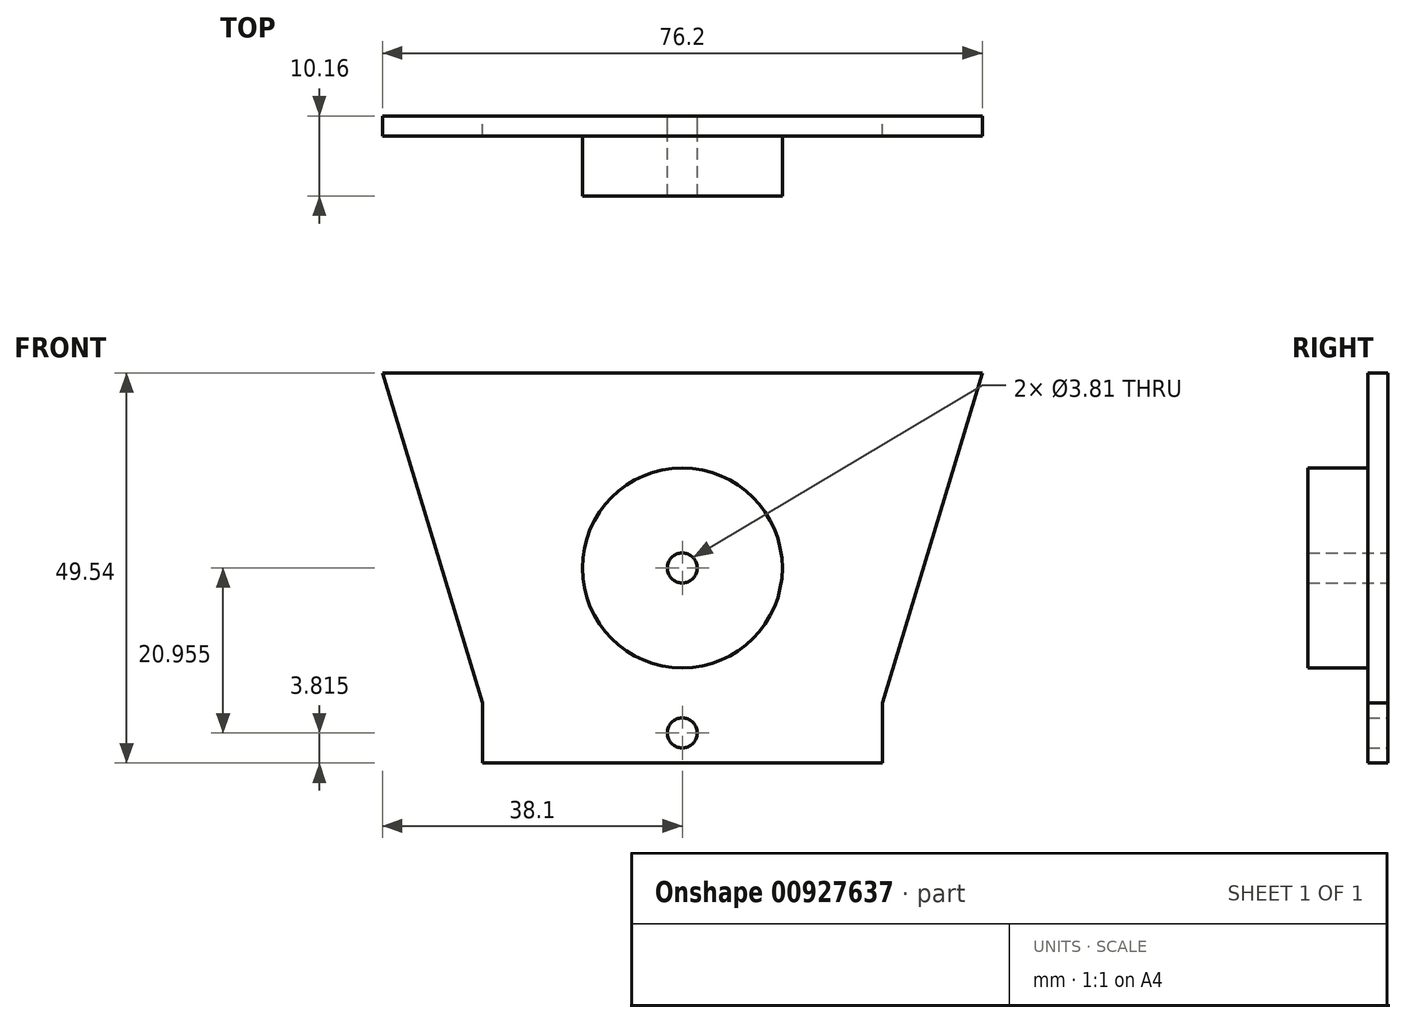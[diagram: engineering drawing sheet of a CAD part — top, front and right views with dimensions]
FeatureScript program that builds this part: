
annotation { "Feature Type Name" : "Feature", "Feature Type Description" : "" }
export const myFeature = defineFeature(function(context is Context, id is Id, definition is map)
    precondition{}
    {
        {
            var Q0;
            Q0=qCreatedBy(makeId("Front.planeOp"),FACE);
            var sketch = newSketch(context, id + "F0", { "sketchPlane" : qUnion([Q0])});
            skLineSegment(sketch, "E0.bottom", {"start": v(25.4, 24.77) * mm, "end": v(-25.4, 24.77) * mm});
            skLineSegment(sketch, "E0.top", {"start": v(25.4, -24.77) * mm, "end": v(-25.4, -24.77) * mm});
            skLineSegment(sketch, "E0.left", {"start": v(25.4, -17.15) * mm, "end": v(25.4, -24.77) * mm});
            skLineSegment(sketch, "E0.right", {"start": v(-25.4, -17.15) * mm, "end": v(-25.4, -24.77) * mm});
            skPoint(sketch, "E0.middle", {"position": v(0, 0) * mm});
            skLineSegment(sketch, "E1", {"start": v(-25.4, -17.15) * mm, "end": v(-38.1, 24.77) * mm});
            skLineSegment(sketch, "E2", {"start": v(-38.1, 24.77) * mm, "end": v(-25.4, 24.77) * mm});
            skLineSegment(sketch, "E3", {"start": v(25.4, -17.15) * mm, "end": v(38.1, 24.77) * mm});
            skLineSegment(sketch, "E4", {"start": v(38.1, 24.76) * mm, "end": v(25.4, 24.76) * mm});
            skCircle(sketch, "E5", {"center": v(0, -20.96) * mm, "radius": 1.9 * mm});
            skCircle(sketch, "E6", {"center": v(0, 0) * mm, "radius": 12.7 * mm});
            skCircle(sketch, "E7", {"center": v(0, 0) * mm, "radius": 1.9 * mm});
            skSolve(sketch);
        }
        {
            var Q0;
            Q0=makeQuery(id+"F0.imprint","IMPRINT",FACE,{"disambiguationData":[TD([[makeQuery(id+"F0.imprint","IMPRINT",EDGE,{"derivedFrom":sQuery(id+"F0.wireOp",EDGE,"E0.bottom")}),1.0]])]});
            extrude(context, id + "F1", {"entities" : qUnion([Q0]), "depth" : 2.54 * mm, "offsetDistance" : 25.4 * mm});
        }
        {
            var Q0;
            Q0=makeQuery(id+"F0.imprint","IMPRINT",FACE,{"disambiguationData":[TD([[makeQuery(id+"F0.imprint","IMPRINT",EDGE,{"derivedFrom":sQuery(id+"F0.wireOp",EDGE,"E6")}),1.0]])]});
            extrude(context, id + "F2", {"entities" : qUnion([Q0]), "operationType" : NewBodyOperationType.ADD, "depth" : 10.16 * mm, "offsetDistance" : 25.4 * mm});
        }
    });
